# Revit family: Kessel 730125.10XR en
name_source: partatom
category: Pipe Accessories
revit_build: Autodesk Revit Architecture 2014 (Build: 20130308_1515(x64)
units: mm (PartAtom-declared; Revit-internal decimal feet)

## types (1)
- Kessel 730125.10XR en
    <1.010.00.2> Number of the part of the guideline = 38
    <1.010.00.3> Issue date (month) of the guideline = 201805
    <1.010.00.4> Manufacturer name = Kessel
    <1.010.00.5> Revision date of the file = 20190228
    <1.800.00.3> BS number = 10000500000000000000000000000300000000200000000017???00001
    <1.800.00.4> Comment field = Staufix backwater valve DN 125, floor slab, tileable, Type 2 R
    <1.810.00.3> Manufacturer’s reference number = 730125.10XR
    <1.810.00.4> DATANORM number = 730125.10XR
    <1.810.00.6> GTIN number = 4026092076453
    <1.960/3L.00.8> Link (URL) = http://www.kessel.de
    <38.100.00.4> Drain type for floor, roof and sanitary objects = Backwater valves
    <38.110.00.4> Floor, roof and sanitary works sequences = Staufix backwater valve
    <38.400.00.3> Material of the drain body = polymer
    <38.500.00.3> Sealing variantion = with glued flange
    <38.700.00.15> Connection to GLT, GA = no
    <38.700.00.16> Fire resistance class can be retrofitted = no
    <38.700.00.4> product name = Staufix backwater valve DN 125, floor slab, tileable, Type 2 R
    <38.700.00.6> Complete article (one-piece) from combination (multi-part design) Drain body and attachment piece = yes
    <38.700.00.7> Potential compensation (ground connection) available = no
    <38.700.00.8> Electrical connection = no
    <38.710.01.10> depth [mm] = 444
    <38.710.01.14> with sound decoupling = no
    <38.710.01.15> Leafy / Kiefang = no
    <38.710.01.3> Product name = Staufix backwater valve DN 125, floor slab, tileable, Type 2 R
    <38.710.01.4> Type = other
    <38.710.01.5> Nominal system = DN
    <38.710.01.6> Nominal dimensions = 125
    <38.710.01.9> installation width [mm] = 511
    <38.710.13.3> Product name = Staufix backwater valve DN 125, floor slab, tileable, Type 2 R
    <38.710.13.4> Variant of the drainage drain = point drain
    <38.710.13.7> Leafy / Kiefang = no
    <38.710.15.3> Product name = tileable cover plate, plastic
    <38.710.15.4> Execution drain grate = tileable cover plate
    <38.710.15.5> Material of the drain grate = plastic
    <38.710.15.6> Fixing the grate = lockable
    <38.710.15.7> Execution of the drain grate = tileable cover plate
    <38.710.15.9> Slip resistance of the drain grate = no
    <38.710.16.3> Type of measurements = external dimensions
    <38.710.16.4> Length = 511
    <38.710.16.5> Width = 444
    CONNECTOR0_DIAMETER_dX_0r = 0 mm  [stored 0 ft]
    CONNECTOR0_dX_01 = 15 mm
    CONNECTOR0_ref_dX = 15 mm
    CONNECTOR1_DIAMETER_dX_0r = 0 mm  [stored 0 ft]
    CONNECTOR1_dX_00 = 436 mm
    CONNECTOR1_dX_01 = 511 mm
    CONNECTOR1_ref_dX = 436 mm
    CONNECTOR1_ref_dZ = 7 mm  [stored 0.0229659 ft]
    Manufacturer = Kessel
    Model = 730125.10XR
    URL = www.kessel.com

note: [stored X ft] marks values corroborated as IEEE doubles in the binary element streams (Revit-internal decimal feet)
